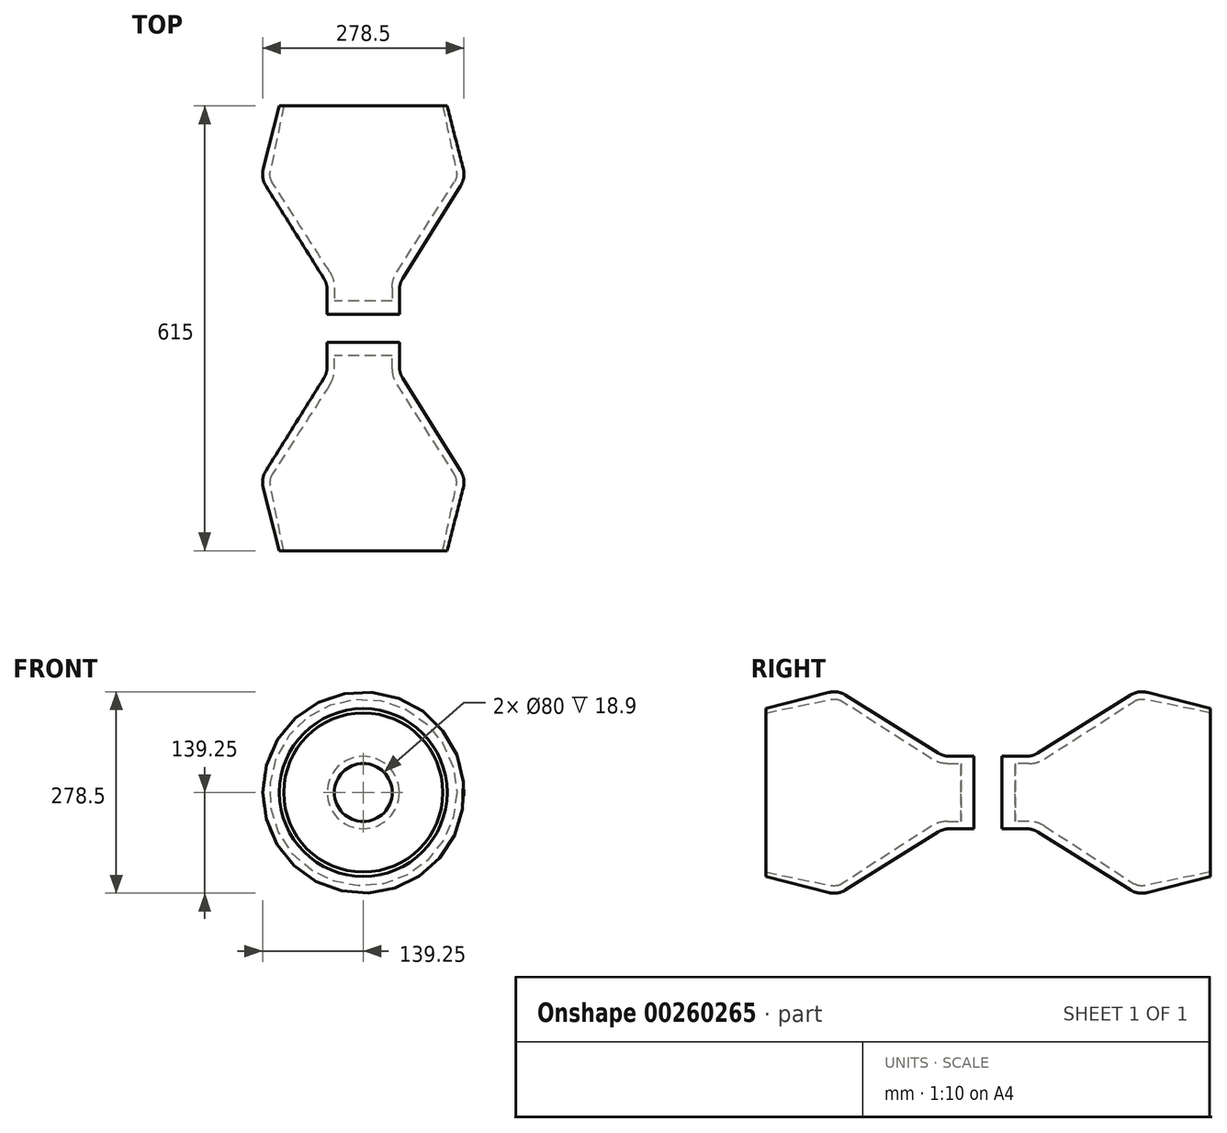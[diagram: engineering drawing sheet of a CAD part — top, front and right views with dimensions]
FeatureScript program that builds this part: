
annotation { "Feature Type Name" : "Feature", "Feature Type Description" : "" }
export const myFeature = defineFeature(function(context is Context, id is Id, definition is map)
    precondition{}
    {
        {
            var Q0;
            Q0=qCreatedBy(makeId("Front.planeOp"),FACE);
            var sketch = newSketch(context, id + "F0", { "sketchPlane" : qUnion([Q0])});
            skLineSegment(sketch, "E0", {"start": v(0, 270) * mm, "end": v(0, 288) * mm});
            skLineSegment(sketch, "E1", {"start": v(0, 288) * mm, "end": v(50, 288) * mm});
            skLineSegment(sketch, "E2", {"start": v(50, 288) * mm, "end": v(50, 246) * mm});
            skLineSegment(sketch, "E3", {"start": v(50, 246) * mm, "end": v(141.5, 99.57) * mm});
            skLineSegment(sketch, "E4", {"start": v(141.5, 99.57) * mm, "end": v(116, 0) * mm});
            skLineSegment(sketch, "E5", {"start": v(116, 0) * mm, "end": v(110, 0) * mm});
            skLineSegment(sketch, "E6", {"start": v(110, 0) * mm, "end": v(130.5, 98.5) * mm});
            skLineSegment(sketch, "E7", {"start": v(130.5, 98.5) * mm, "end": v(40, 239.36) * mm});
            skLineSegment(sketch, "E8", {"start": v(40, 239.36) * mm, "end": v(40, 270) * mm});
            skLineSegment(sketch, "E9", {"start": v(40, 270) * mm, "end": v(0, 270) * mm});
            skLineSegment(sketch, "E10", {"start": v(0, 270) * mm, "end": v(0, 0) * mm, "construction": true});
            skCircle(sketch, "E11", {"center": v(109.25, 94.57) * mm, "radius": 20 * mm, "construction": true});
            skCircle(sketch, "E12", {"center": v(109.25, 94.57) * mm, "radius": 30 * mm, "construction": true});
            skLineSegment(sketch, "E13", {"start": v(0, 230) * mm, "end": v(46.01, 230) * mm, "construction": true});
            skLineSegment(sketch, "E14", {"start": v(85.25, 168.93) * mm, "end": v(98.16, 168.93) * mm, "construction": true});
            skSolve(sketch);
        }
        {
            var Q0;
            Q0=makeQuery(id+"F0.imprint","IMPRINT",FACE,{"disambiguationData":[TD([[makeQuery(id+"F0.imprint","IMPRINT",EDGE,{"derivedFrom":sQuery(id+"F0.wireOp",EDGE,"E0")}),-1.0]])]});
            var Q1;
            Q1=sQuery(id+"F0.wireOp",EDGE,"E10");
            revolve(context, id + "F1", {"entities" : qUnion([Q0]), "axis" : qUnion([Q1]), "revolveType" : RevolveType.FULL});
        }
        {
            var Q0;
            Q0=makeQuery(id+"F1.opRevolve","SWEPT_EDGE",EDGE,{"disambiguationData":[OSD([sQuery(id+"F0.wireOp",EDGE,"E6"),sQuery(id+"F0.wireOp",EDGE,"E7")])]});
            fillet(context, id + "F2", {"entities" : qUnion([Q0]), "radius" : 20 * mm, "tangentPropagation" : true, "defaultsChanged" : false, "vertexSettings" : [], "allowEdgeOverflow" : false});
        }
        {
            var Q0;
            Q0=makeQuery(id+"F1.opRevolve","SWEPT_EDGE",EDGE,{"disambiguationData":[OSD([sQuery(id+"F0.wireOp",EDGE,"E3"),sQuery(id+"F0.wireOp",EDGE,"E4")])]});
            var Q1;
            Q1=makeQuery(id+"F1.opRevolve","SWEPT_EDGE",EDGE,{"disambiguationData":[OSD([sQuery(id+"F0.wireOp",EDGE,"E2"),sQuery(id+"F0.wireOp",EDGE,"E3")])]});
            fillet(context, id + "F3", {"entities" : qUnion([Q0, Q1]), "radius" : 30 * mm, "tangentPropagation" : true, "defaultsChanged" : false, "vertexSettings" : [], "allowEdgeOverflow" : false});
        }
        {
            var Q0;
            Q0=makeQuery(id+"F1.opRevolve","SWEPT_EDGE",EDGE,{"disambiguationData":[OSD([sQuery(id+"F0.wireOp",EDGE,"E7"),sQuery(id+"F0.wireOp",EDGE,"E8")])]});
            fillet(context, id + "F4", {"entities" : qUnion([Q0]), "radius" : 40 * mm, "tangentPropagation" : true, "allowEdgeOverflow" : false});
        }
        {
            var Q0;
            Q0=qCreatedBy(makeId("Top.planeOp"),FACE);
            var sketch = newSketch(context, id + "F5", { "sketchPlane" : qUnion([Q0])});
            skLineSegment(sketch, "E15", {"start": v(0, 0) * mm, "end": v(116, 0) * mm});
            skLineSegment(sketch, "E16", {"start": v(0, 0) * mm, "end": v(0, -116) * mm});
            skSolve(sketch);
        }
        {
            var Q0;
            Q0=makeQuery(id+"F1.opRevolve","SWEPT_BODY",BODY,{"disambiguationData":[OSD([sQuery(id+"F0.wireOp",EDGE,"E0"),sQuery(id+"F0.wireOp",EDGE,"E1"),sQuery(id+"F0.wireOp",EDGE,"E2"),sQuery(id+"F0.wireOp",EDGE,"E3"),sQuery(id+"F0.wireOp",EDGE,"E4"),sQuery(id+"F0.wireOp",EDGE,"E5"),sQuery(id+"F0.wireOp",EDGE,"E6"),sQuery(id+"F0.wireOp",EDGE,"E7"),sQuery(id+"F0.wireOp",EDGE,"E8"),sQuery(id+"F0.wireOp",EDGE,"E9")])]});
            var Q1;
            Q1=sQuery(id+"F5.wireOp",EDGE,"E15");
            transform(context, id + "F6", {"entities" : qUnion([Q0]), "transformType" : TransformType.ROTATION, "transformAxis" : qUnion([Q1]), "angle" : 180 * degree, "makeCopy" : false});
        }
        {
            var Q0;
            Q0=makeQuery(id+"F1.opRevolve","SWEPT_BODY",BODY,{"disambiguationData":[OSD([sQuery(id+"F0.wireOp",EDGE,"E0"),sQuery(id+"F0.wireOp",EDGE,"E1"),sQuery(id+"F0.wireOp",EDGE,"E2"),sQuery(id+"F0.wireOp",EDGE,"E3"),sQuery(id+"F0.wireOp",EDGE,"E4"),sQuery(id+"F0.wireOp",EDGE,"E5"),sQuery(id+"F0.wireOp",EDGE,"E6"),sQuery(id+"F0.wireOp",EDGE,"E7"),sQuery(id+"F0.wireOp",EDGE,"E8"),sQuery(id+"F0.wireOp",EDGE,"E9")])]});
            transform(context, id + "F7", {"entities" : qUnion([Q0]), "transformType" : TransformType.TRANSLATION_3D, "dx" : (320 / 2) * mm, "dy" : (320 / 2) * mm, "dz" : 300 * mm, "makeCopy" : false});
        }
        {
            var Q0;
            Q0=makeQuery(id+"F1.opRevolve","SWEPT_BODY",BODY,{"disambiguationData":[OSD([sQuery(id+"F0.wireOp",EDGE,"E0"),sQuery(id+"F0.wireOp",EDGE,"E1"),sQuery(id+"F0.wireOp",EDGE,"E2"),sQuery(id+"F0.wireOp",EDGE,"E3"),sQuery(id+"F0.wireOp",EDGE,"E4"),sQuery(id+"F0.wireOp",EDGE,"E5"),sQuery(id+"F0.wireOp",EDGE,"E6"),sQuery(id+"F0.wireOp",EDGE,"E7"),sQuery(id+"F0.wireOp",EDGE,"E8"),sQuery(id+"F0.wireOp",EDGE,"E9")])]});
            transform(context, id + "F8", {"entities" : qUnion([Q0]), "transformType" : TransformType.TRANSLATION_3D, "dx" : 0 * mm, "dy" : 0 * mm, "dz" : -12 * mm, "makeCopy" : false});
        }
        {
            var Q0;
            Q0=makeQuery(id+"F1.opRevolve","SWEPT_BODY",BODY,{"disambiguationData":[OSD([sQuery(id+"F0.wireOp",EDGE,"E0"),sQuery(id+"F0.wireOp",EDGE,"E1"),sQuery(id+"F0.wireOp",EDGE,"E2"),sQuery(id+"F0.wireOp",EDGE,"E3"),sQuery(id+"F0.wireOp",EDGE,"E4"),sQuery(id+"F0.wireOp",EDGE,"E5"),sQuery(id+"F0.wireOp",EDGE,"E6"),sQuery(id+"F0.wireOp",EDGE,"E7"),sQuery(id+"F0.wireOp",EDGE,"E8"),sQuery(id+"F0.wireOp",EDGE,"E9")])]});
            var Q1;
            Q1=sQuery(id+"F5.wireOp",EDGE,"E15");
            transform(context, id + "F9", {"entities" : qUnion([Q0]), "transformType" : TransformType.ROTATION, "transformAxis" : qUnion([Q1]), "angle" : 90 * degree, "oppositeDirection" : true, "makeCopy" : false});
        }
        {
            var Q0;
            Q0=makeQuery(id+"F1.opRevolve","SWEPT_BODY",BODY,{"disambiguationData":[OSD([sQuery(id+"F0.wireOp",EDGE,"E0"),sQuery(id+"F0.wireOp",EDGE,"E1"),sQuery(id+"F0.wireOp",EDGE,"E2"),sQuery(id+"F0.wireOp",EDGE,"E3"),sQuery(id+"F0.wireOp",EDGE,"E4"),sQuery(id+"F0.wireOp",EDGE,"E5"),sQuery(id+"F0.wireOp",EDGE,"E6"),sQuery(id+"F0.wireOp",EDGE,"E7"),sQuery(id+"F0.wireOp",EDGE,"E8"),sQuery(id+"F0.wireOp",EDGE,"E9")])]});
            transform(context, id + "F10", {"entities" : qUnion([Q0]), "transformType" : TransformType.TRANSLATION_3D, "dx" : 15 * mm, "dy" : 315 * mm, "dz" : 360 * mm, "makeCopy" : false});
        }
        {
            var Q0;
            Q0=makeQuery(id+"F1.opRevolve","SWEPT_FACE",FACE,{"disambiguationData":[OSD([sQuery(id+"F0.wireOp",EDGE,"E1")])]});
            cPlane(context, id + "F12", {"entities" : qUnion([Q0]), "cplaneType" : CPlaneType.OFFSET, "offset" : (39 / 2) * mm, "width" : 150 * mm, "height" : 150 * mm});
        }
        {
            var Q0;
            Q0=makeQuery(id+"F1.opRevolve","SWEPT_BODY",BODY,{"disambiguationData":[OSD([sQuery(id+"F0.wireOp",EDGE,"E0"),sQuery(id+"F0.wireOp",EDGE,"E1"),sQuery(id+"F0.wireOp",EDGE,"E2"),sQuery(id+"F0.wireOp",EDGE,"E3"),sQuery(id+"F0.wireOp",EDGE,"E4"),sQuery(id+"F0.wireOp",EDGE,"E5"),sQuery(id+"F0.wireOp",EDGE,"E6"),sQuery(id+"F0.wireOp",EDGE,"E7"),sQuery(id+"F0.wireOp",EDGE,"E8"),sQuery(id+"F0.wireOp",EDGE,"E9")])]});
            var Q1;
            Q1=qCreatedBy(id+"F12.planeOp",FACE);
            mirror(context, id + "F13", {"entities" : qUnion([Q0]), "mirrorPlane" : qUnion([Q1])});
        }
    });
